# Revit family: Sink-Wall_Mount-Lavatory-KOHLER-Kelston-K-24051
name_source: partatom
category: Plumbing Fixtures
units: mm (PartAtom-declared; Revit-internal decimal feet)

## family parameters
Cut with Voids When Loaded = No
Host = Face
OmniClass Number = 23.31.13.00
OmniClass Title = Sinks
Part Type = Normal
Room Calculation Point = No
Round Connector Dimension = Use Diameter
Shared = No

## types (6) — shared parameters
ADA Compliant = No
Assembly Code = D2010400
CW Connection = No
Cold Water Inlet = Cold Water Inlet
Date Modified = 07/25/2022
Default Elevation = 36"
Drain Included = Yes
HW Connection = No
Height = 6 15/16"
Hot Water Inlet = Hot Water Inlet
Length = 24"
Manufacturer = Kohler Co.
Master Format 2014 = 22 41 16
Master Format 2014 Name = Residential Lavatories and Sinks
Material = Vitreous China
Product Documentation Link = https://www.us.kohler.com
Product Name = Kelston
Product Page URL = http://www.us.kohler.com
URL = https://www.us.kohler.com
Vent Connection = No
Waste Connection = Yes
Waste Water Outlet = Waste Water Outlet
WaterSense Certified = No
Width = 20"

## per-type parameters (varying)
| type | 4" Faucet Hole Spacing | 8" Faucet Hole Spacing | Description | Faucet Hole Spacing | Finish | Model | Type |
| 4" Faucet Hole Spacing, 0-White | Yes | No | Pedestal bathroom sink with 4inch centerset faucet holes | 4" | Kohler-Vitreous_China-0-White | K-24051-4-0 | 1 |
| 4" Faucet Hole Spacing, 7-Black Black | Yes | No | Pedestal bathroom sink with 4inch centerset faucet holes | 4" | Kohler-Vitreous_China-7-Black_Black | K-24051-4-7 | 2 |
| 4" Faucet Hole Spacing, 96-Biscuit | Yes | No | Pedestal bathroom sink with 4inch centerset faucet holes | 4" | Kohler-Vitreous_China-96-Biscuit | K-24051-4-96 | 3 |
| 8" Faucet Hole Spacing, 0-White | No | Yes | Pedestal bathroom sink with 8inch widespread faucet holes | 8" | Kohler-Vitreous_China-0-White | K-24051-8-0 | 4 |
| 8" Faucet Hole Spacing, 7-Black Black | No | Yes | Pedestal bathroom sink with 8inch widespread faucet holes | 8" | Kohler-Vitreous_China-7-Black_Black | K-24051-8-7 | 5 |
| 8" Faucet Hole Spacing, 96-Biscuit | No | Yes | Pedestal bathroom sink with 8inch widespread faucet holes | 8" | Kohler-Vitreous_China-96-Biscuit | K-24051-8-96 | 6 |

## geometry (parser evidence)
native form markers: Sweep x5
no freeform markers — native parametric forms only
